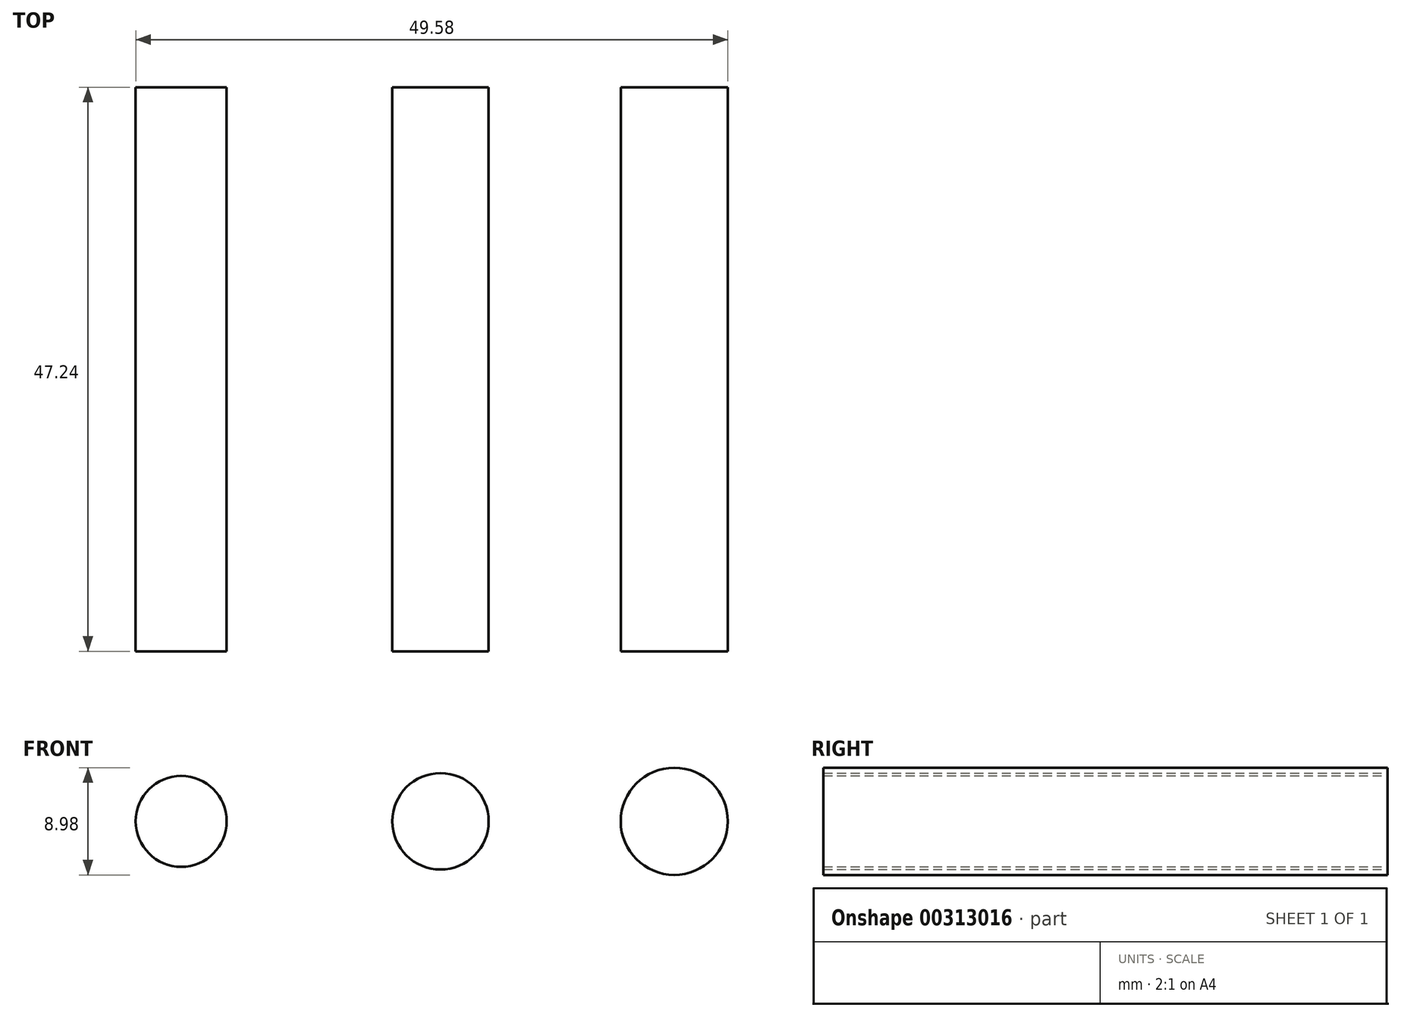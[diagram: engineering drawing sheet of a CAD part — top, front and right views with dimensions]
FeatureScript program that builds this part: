
annotation { "Feature Type Name" : "Feature", "Feature Type Description" : "" }
export const myFeature = defineFeature(function(context is Context, id is Id, definition is map)
    precondition{}
    {
        {
            var Q0;
            Q0=qCreatedBy(makeId("Front.planeOp"),FACE);
            var sketch = newSketch(context, id + "F0", { "sketchPlane" : qUnion([Q0])});
            skCircle(sketch, "E0", {"center": v(0, 0) * mm, "radius": 4.03 * mm});
            skCircle(sketch, "E1", {"center": v(-21.71, 0) * mm, "radius": 3.81 * mm});
            skCircle(sketch, "E2", {"center": v(19.57, 0) * mm, "radius": 4.49 * mm});
            skSolve(sketch);
        }
        {
            var Q0;
            Q0 = qSketchRegion(id + "F0", true);
            extrude(context, id + "F1", {"entities" : qUnion([Q0]), "depth" : 47.24 * mm});
        }
    });
